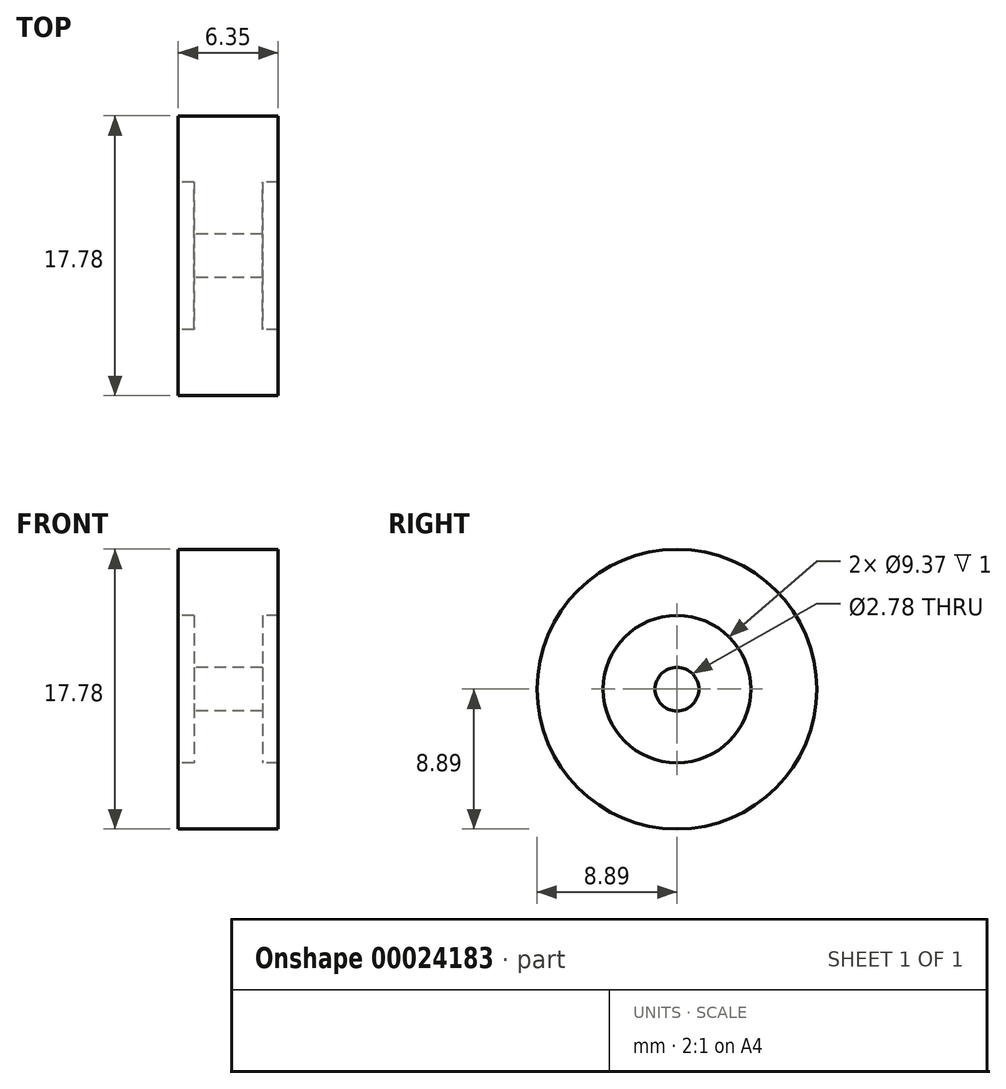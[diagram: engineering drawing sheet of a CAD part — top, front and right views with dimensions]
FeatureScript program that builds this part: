
annotation { "Feature Type Name" : "Feature", "Feature Type Description" : "" }
export const myFeature = defineFeature(function(context is Context, id is Id, definition is map)
    precondition{}
    {
        {
            var Q0;
            Q0=qCreatedBy(makeId("Front.planeOp"),FACE);
            var sketch = newSketch(context, id + "F0", { "sketchPlane" : qUnion([Q0])});
            skLineSegment(sketch, "E0", {"start": v(0, 0) * mm, "end": v(14.1, 0) * mm, "construction": true});
            skLineSegment(sketch, "E1.top", {"start": v(2.43, 1.39) * mm, "end": v(6.78, 1.39) * mm});
            skLineSegment(sketch, "E2.top", {"start": v(2.43, 8.88) * mm, "end": v(6.78, 8.88) * mm});
            skLineSegment(sketch, "E2.left", {"start": v(2.43, 1.39) * mm, "end": v(2.43, 4.68) * mm});
            skLineSegment(sketch, "E2.right", {"start": v(6.78, 1.39) * mm, "end": v(6.78, 4.68) * mm});
            skLineSegment(sketch, "E3.bottom", {"start": v(1.43, 4.68) * mm, "end": v(7.78, 4.68) * mm});
            skLineSegment(sketch, "E3.top", {"start": v(1.43, 8.88) * mm, "end": v(7.78, 8.88) * mm});
            skLineSegment(sketch, "E3.left", {"start": v(1.43, 8.88) * mm, "end": v(1.43, 4.68) * mm});
            skLineSegment(sketch, "E3.right", {"start": v(7.78, 8.88) * mm, "end": v(7.78, 4.68) * mm});
            skPoint(sketch, "E4.orphan", {"position": v(7.78, 1.39) * mm});
            skPoint(sketch, "E5.orphan", {"position": v(1.43, 1.39) * mm});
            skSolve(sketch);
        }
        {
            var Q0;
            {var subQ1=sQuery(id+"F0.wireOp",EDGE,"E3.left");Q0=makeQuery(id+"F0.imprint","IMPRINT",FACE,{"disambiguationData":[TD([[makeQuery(id+"F0.imprint","IMPRINT",EDGE,{"derivedFrom":subQ1}),1.0]])]});}
            var Q1;
            Q1=makeQuery(id+"F0.imprint","IMPRINT",FACE,{"disambiguationData":[TD([[makeQuery(id+"F0.imprint","IMPRINT",EDGE,{"derivedFrom":sQuery(id+"F0.wireOp",EDGE,"E1.bottom")}),1.0]])]});
            var Q2;
            Q2=makeQuery(id+"F0.imprint","IMPRINT",FACE,{"disambiguationData":[TD([[makeQuery(id+"F0.imprint","IMPRINT",EDGE,{"derivedFrom":sQuery(id+"F0.wireOp",EDGE,"E1.top")}),1.0]])]});
            var Q3;
            Q3=sQuery(id+"F0.wireOp",EDGE,"E0");
            revolve(context, id + "F1", {"entities" : qUnion([Q0, Q1, Q2]), "axis" : qUnion([Q3]), "revolveType" : RevolveType.FULL});
        }
    });
